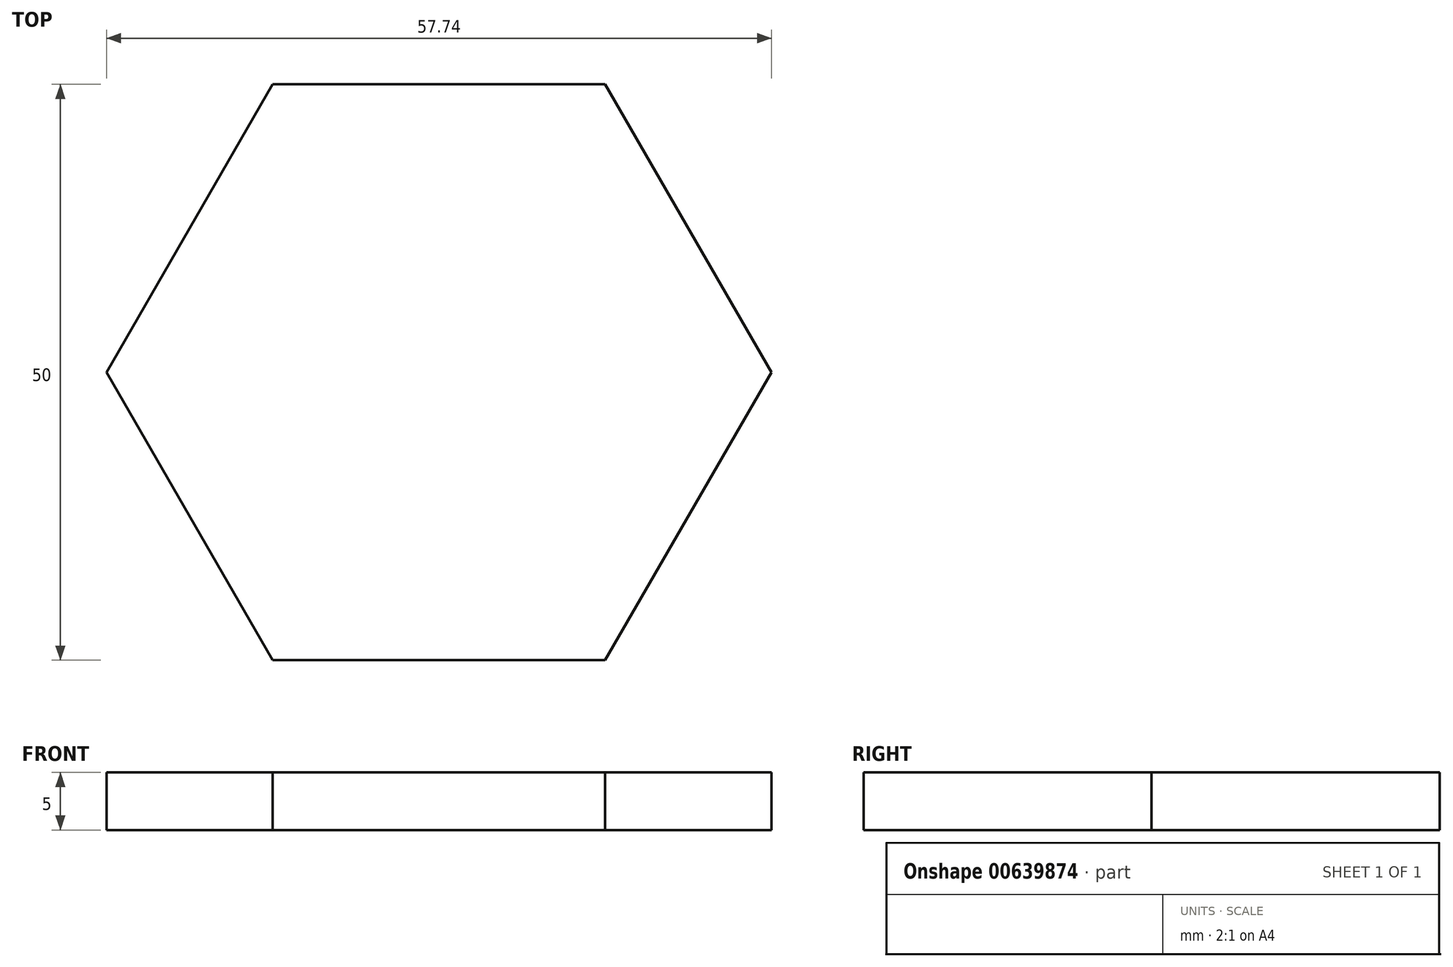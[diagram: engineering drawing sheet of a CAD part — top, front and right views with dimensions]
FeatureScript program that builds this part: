
annotation { "Feature Type Name" : "Feature", "Feature Type Description" : "" }
export const myFeature = defineFeature(function(context is Context, id is Id, definition is map)
    precondition{}
    {
        {
            var Q0;
            Q0=qCreatedBy(makeId("Top.planeOp"),FACE);
            var sketch = newSketch(context, id + "F0", { "sketchPlane" : qUnion([Q0])});
            skCircle(sketch, "E0.cCircle", {"center": v(0, 0) * mm, "radius": 25 * mm, "construction": true});
            skLineSegment(sketch, "E0.0", {"start": v(-14.43, 25) * mm, "end": v(14.43, 25) * mm});
            skLineSegment(sketch, "E0.1", {"start": v(14.43, 25) * mm, "end": v(28.87, 0) * mm});
            skLineSegment(sketch, "E0.2", {"start": v(28.87, 0) * mm, "end": v(14.43, -25) * mm});
            skLineSegment(sketch, "E0.3", {"start": v(14.43, -25) * mm, "end": v(-14.43, -25) * mm});
            skLineSegment(sketch, "E0.4", {"start": v(-14.43, -25) * mm, "end": v(-28.87, 0) * mm});
            skLineSegment(sketch, "E0.5", {"start": v(-28.87, 0) * mm, "end": v(-14.43, 25) * mm});
            skPoint(sketch, "E0.0.midPoint", {"position": v(0, 25) * mm});
            skSolve(sketch);
        }
        {
            var Q0;
            Q0=makeQuery(id+"F0.imprint","IMPRINT",FACE,{"disambiguationData":[TD([[makeQuery(id+"F0.imprint","IMPRINT",EDGE,{"derivedFrom":sQuery(id+"F0.wireOp",EDGE,"E0.0")}),-1.0]])]});
            extrude(context, id + "F1", {"entities" : qUnion([Q0]), "depth" : 5 * mm, "offsetDistance" : 25 * mm});
        }
    });
